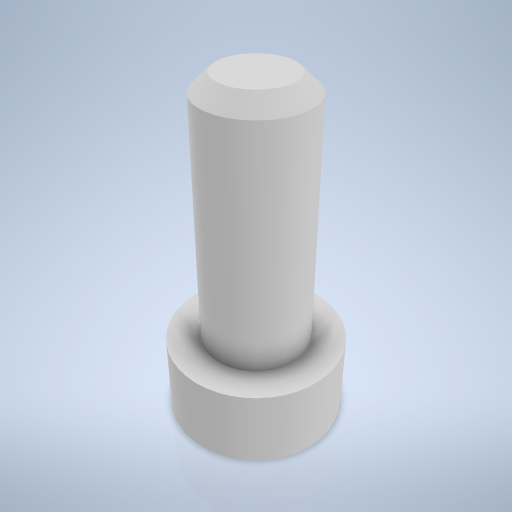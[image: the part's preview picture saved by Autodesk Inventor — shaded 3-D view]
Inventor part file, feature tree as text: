
AUTODESK INVENTOR PART (.ipt)
format: ipt  version: 2024.2 (Build 282272000, 272)  size: 251,392 bytes
history: native  units: mm
features: revolve x1, chamfer x1, sketch x1
ambient origin geometry x8: Origin, YZ Plane, XZ Plane, XY Plane, X Axis, Y Axis, Z Axis, Center Point
bodies: Volumenkörper1 (feature_tree)
feature tree (3):
  revolve  "Umdrehung1"
  chamfer  "Fasen1"  Distance=10.5mm
  sketch  "Skizze1"  dims[d0=6.5mm d1=10.5mm d2=21.0mm d3=16.0mm d4=90.0deg d5=1.0mm d6=2.0mm d7=45.0deg]
